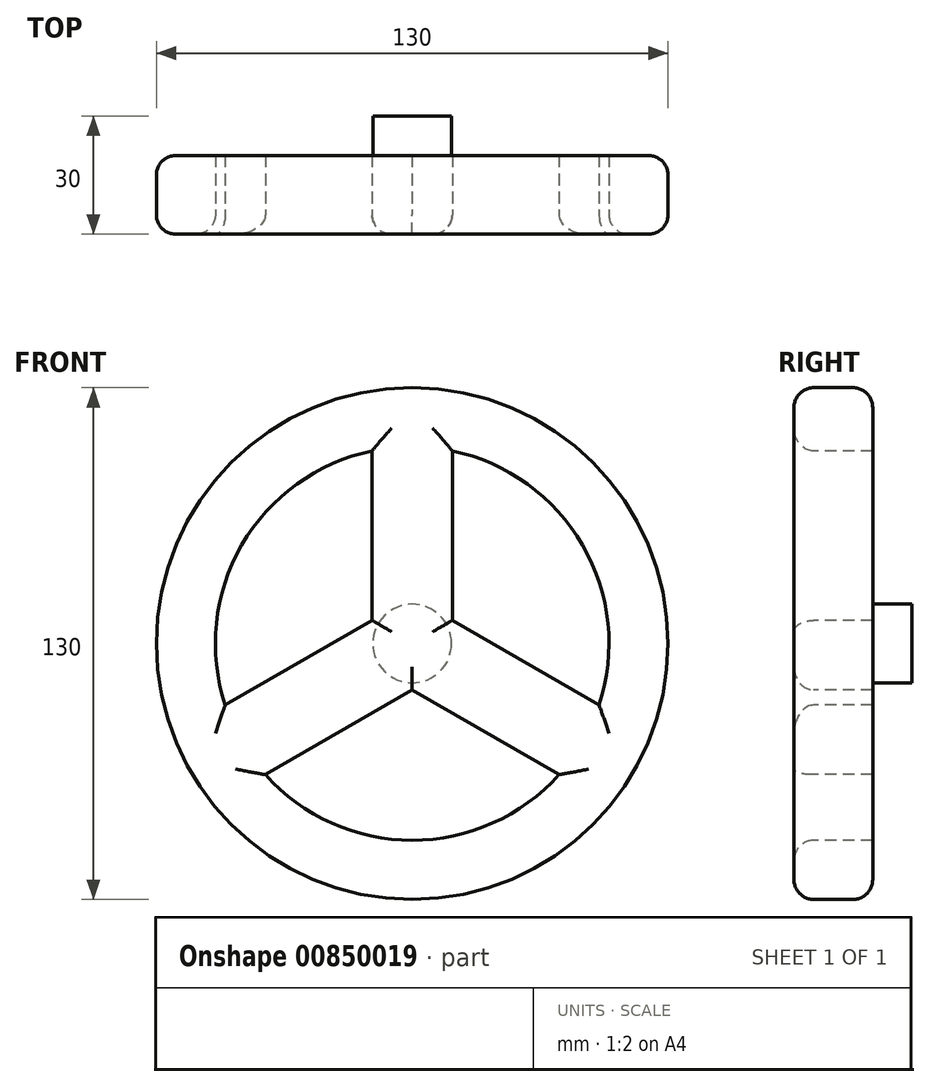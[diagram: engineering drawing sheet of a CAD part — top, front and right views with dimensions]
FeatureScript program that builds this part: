
annotation { "Feature Type Name" : "Feature", "Feature Type Description" : "" }
export const myFeature = defineFeature(function(context is Context, id is Id, definition is map)
    precondition{}
    {
        {
            var Q0;
            Q0=qCreatedBy(makeId("Front.planeOp"),FACE);
            var sketch = newSketch(context, id + "F0", { "sketchPlane" : qUnion([Q0])});
            skCircle(sketch, "E0", {"center": v(0, 0) * mm, "radius": 10 * mm});
            skSolve(sketch);
        }
        {
            var Q0;
            Q0=makeQuery(id+"F0.imprint","IMPRINT",FACE,{"disambiguationData":[TD([[makeQuery(id+"F0.imprint","IMPRINT",EDGE,{"derivedFrom":sQuery(id+"F0.wireOp",EDGE,"E0")}),1.0]])]});
            extrude(context, id + "F1", {"entities" : qUnion([Q0]), "depth" : 10 * mm, "offsetDistance" : 25 * mm});
        }
        {
            var Q0;
            Q0=qCreatedBy(makeId("Front.planeOp"),FACE);
            cPlane(context, id + "F2", {"entities" : qUnion([Q0]), "cplaneType" : CPlaneType.OFFSET, "offset" : 30 * mm, "width" : 150 * mm, "height" : 150 * mm});
        }
        {
            var Q0;
            Q0=qCreatedBy(id+"F2.planeOp",FACE);
            var sketch = newSketch(context, id + "F3", { "sketchPlane" : qUnion([Q0])});
            skCircle(sketch, "E1", {"center": v(0, 0) * mm, "radius": 65 * mm});
            skSolve(sketch);
        }
        {
            var Q0;
            Q0=makeQuery(id+"F3.imprint","IMPRINT",FACE,{"disambiguationData":[TD([[makeQuery(id+"F3.imprint","IMPRINT",EDGE,{"derivedFrom":sQuery(id+"F3.wireOp",EDGE,"E1")}),1.0]])]});
            var Q1;
            Q1=makeQuery(id+"F1.opExtrude","CAP_FACE",FACE,{"disambiguationData":[OSD([sQuery(id+"F0.wireOp",EDGE,"E0")])],"isStart":false});
            extrude(context, id + "F4", {"entities" : qUnion([Q0]), "operationType" : NewBodyOperationType.ADD, "endBound" : BoundingType.UP_TO_SURFACE, "oppositeDirection" : true, "depth" : 25 * mm, "endBoundEntityFace" : qUnion([Q1]), "offsetDistance" : 25 * mm});
        }
        {
            var Q0;
            Q0=makeQuery(id+"F4.opExtrude","CAP_FACE",FACE,{"disambiguationData":[OSD([sQuery(id+"F3.wireOp",EDGE,"E1")])],"isStart":true});
            var sketch = newSketch(context, id + "F5", { "sketchPlane" : qUnion([Q0])});
            skLineSegment(sketch, "E2", {"start": v(10.19, 5) * mm, "end": v(10.19, 48.95) * mm});
            skLineSegment(sketch, "E3", {"start": v(-10.19, 5) * mm, "end": v(-10.19, 48.95) * mm});
            skArc(sketch, "E4", {"start": v(-37.3, -33.3) * mm, "mid": v(0, -50) * mm, "end": v(37.3, -33.3) * mm});
            skLineSegment(sketch, "E5.1.0", {"start": v(0.76, -11.32) * mm, "end": v(-37.3, -33.3) * mm});
            skLineSegment(sketch, "E5.1.1", {"start": v(-9.42, 6.32) * mm, "end": v(-47.49, -15.65) * mm});
            skLineSegment(sketch, "E5.2.0", {"start": v(9.42, 6.32) * mm, "end": v(47.49, -15.65) * mm});
            skLineSegment(sketch, "E5.2.1", {"start": v(-0.76, -11.32) * mm, "end": v(37.3, -33.3) * mm});
            skPoint(sketch, "E6.orphan", {"position": v(-60.7, -23.27) * mm});
            skPoint(sketch, "E7.orphan", {"position": v(-50.5, -40.92) * mm});
            skArc(sketch, "E8.trimOffspring", {"start": v(47.49, -15.65) * mm, "mid": v(43.3, 25) * mm, "end": v(10.19, 48.95) * mm});
            skPoint(sketch, "E9.orphan", {"position": v(50.5, -40.92) * mm});
            skPoint(sketch, "E10.orphan", {"position": v(60.7, -23.27) * mm});
            skPoint(sketch, "E11.orphan", {"position": v(10.19, 64.2) * mm});
            skArc(sketch, "E12.trimOffspring", {"start": v(-10.19, 48.95) * mm, "mid": v(-43.3, 25) * mm, "end": v(-47.49, -15.65) * mm});
            skPoint(sketch, "E13.orphan", {"position": v(-10.19, 64.2) * mm});
            skSolve(sketch);
        }
        {
            var Q0;
            Q0=makeQuery(id+"F5.imprint","IMPRINT",FACE,{"disambiguationData":[TD([[makeQuery(id+"F5.imprint","IMPRINT",EDGE,{"derivedFrom":sQuery(id+"F5.wireOp",EDGE,"E3")}),1.0]])]});
            var Q1;
            Q1=makeQuery(id+"F5.imprint","IMPRINT",FACE,{"disambiguationData":[TD([[makeQuery(id+"F5.imprint","IMPRINT",EDGE,{"derivedFrom":sQuery(id+"F5.wireOp",EDGE,"E2")}),-1.0]])]});
            var Q2;
            Q2=makeQuery(id+"F5.imprint","IMPRINT",FACE,{"disambiguationData":[TD([[makeQuery(id+"F5.imprint","IMPRINT",EDGE,{"derivedFrom":sQuery(id+"F5.wireOp",EDGE,"E4")}),1.0]])]});
            extrude(context, id + "F6", {"entities" : qUnion([Q0, Q1, Q2]), "operationType" : NewBodyOperationType.REMOVE, "endBound" : BoundingType.UP_TO_NEXT, "oppositeDirection" : true, "depth" : 25 * mm, "offsetDistance" : 25 * mm});
        }
        {
            var Q0;
            Q0=makeQuery(id+"F4.opExtrude","CAP_FACE",FACE,{"disambiguationData":[OSD([sQuery(id+"F3.wireOp",EDGE,"E1")])],"isStart":true});
            var Q1;
            Q1=makeQuery(id+"F4.opExtrude","SWEPT_FACE",FACE,{"disambiguationData":[OSD([sQuery(id+"F3.wireOp",EDGE,"E1")])]});
            fillet(context, id + "F7", {"entities" : qUnion([Q0, Q1]), "radius" : 5 * mm, "tangentPropagation" : true, "allowEdgeOverflow" : false});
        }
    });
